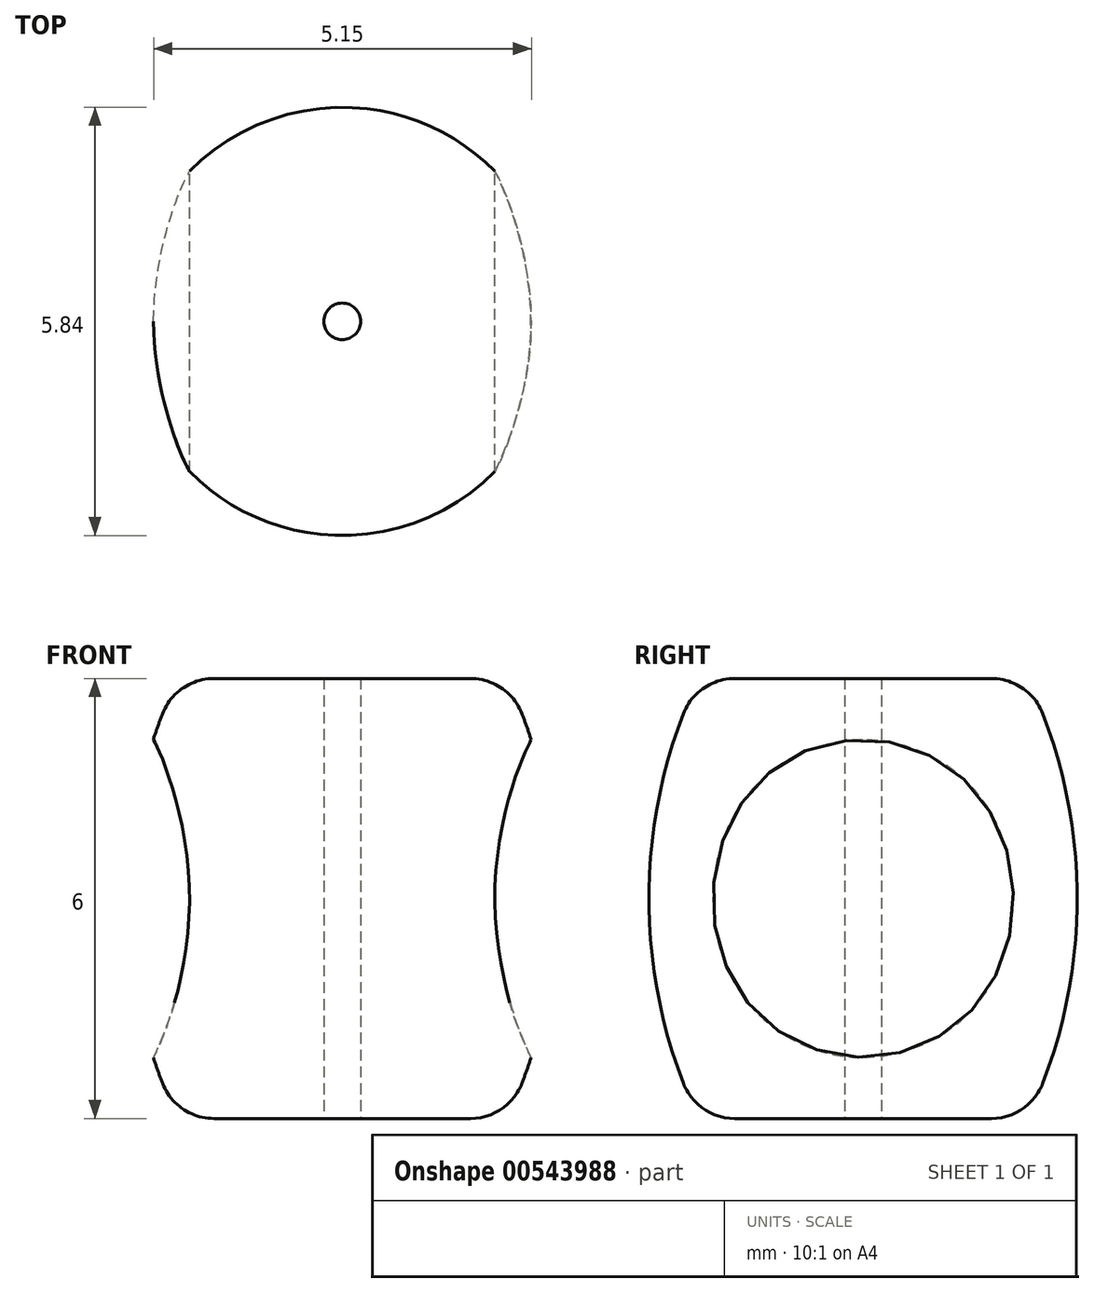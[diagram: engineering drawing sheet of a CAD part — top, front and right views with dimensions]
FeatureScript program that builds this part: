
annotation { "Feature Type Name" : "Feature", "Feature Type Description" : "" }
export const myFeature = defineFeature(function(context is Context, id is Id, definition is map)
    precondition{}
    {
        {
            var Q0;
            Q0=qCreatedBy(makeId("Front.planeOp"),FACE);
            var sketch = newSketch(context, id + "F0", { "sketchPlane" : qUnion([Q0])});
            skLineSegment(sketch, "E0", {"start": v(0.25, 0) * mm, "end": v(0.25, 6) * mm});
            skLineSegment(sketch, "E1", {"start": v(0.25, 0) * mm, "end": v(1.75, 0) * mm});
            skArc(sketch, "E2", {"start": v(1.75, 0) * mm, "mid": v(2.17, 0.13) * mm, "end": v(2.45, 0.48) * mm});
            skLineSegment(sketch, "E3", {"start": v(0, 0) * mm, "end": v(0, 8.8) * mm});
            skArc(sketch, "E4", {"start": v(2.45, 0.48) * mm, "mid": v(2.92, 3) * mm, "end": v(2.45, 5.52) * mm});
            skLineSegment(sketch, "E5", {"start": v(0.25, 6) * mm, "end": v(1.75, 6) * mm});
            skArc(sketch, "E6", {"start": v(1.75, 6) * mm, "mid": v(2.17, 5.87) * mm, "end": v(2.45, 5.52) * mm});
            skLineSegment(sketch, "E7", {"start": v(1.75, 0) * mm, "end": v(1.75, 6) * mm, "construction": true});
            skSolve(sketch);
        }
        {
            var Q0;
            Q0=makeQuery(id+"F0.imprint","IMPRINT",FACE,{"disambiguationData":[TD([[makeQuery(id+"F0.imprint","IMPRINT",EDGE,{"derivedFrom":sQuery(id+"F0.wireOp",EDGE,"E0")}),-1.0]])]});
            var Q1;
            Q1=sQuery(id+"F0.wireOp",EDGE,"E3");
            revolve(context, id + "F1", {"entities" : qUnion([Q0]), "axis" : qUnion([Q1]), "revolveType" : RevolveType.FULL});
        }
        {
            var Q0;
            Q0=qCreatedBy(makeId("Front.planeOp"),FACE);
            var sketch = newSketch(context, id + "F2", { "sketchPlane" : qUnion([Q0])});
            skArc(sketch, "E8", {"start": v(2.75, 5.5) * mm, "mid": v(2.08, 3) * mm, "end": v(2.75, 0.5) * mm});
            skLineSegment(sketch, "E9", {"start": v(2.75, 5.5) * mm, "end": v(2.75, 0.5) * mm, "construction": true});
            skLineSegment(sketch, "E10", {"start": v(2.75, 5.5) * mm, "end": v(3.75, 5.5) * mm});
            skLineSegment(sketch, "E11", {"start": v(3.75, 5.5) * mm, "end": v(3.75, 0.5) * mm});
            skLineSegment(sketch, "E12", {"start": v(3.75, 0.5) * mm, "end": v(2.75, 0.5) * mm});
            skSolve(sketch);
        }
        {
            var Q0;
            Q0=makeQuery(id+"F2.imprint","IMPRINT",FACE,{"disambiguationData":[TD([[makeQuery(id+"F2.imprint","IMPRINT",EDGE,{"derivedFrom":sQuery(id+"F2.wireOp",EDGE,"E8")}),1.0]])]});
            extrude(context, id + "F3", {"entities" : qUnion([Q0]), "depth" : 3 * mm, "offsetDistance" : 25 * mm, "hasSecondDirection" : true, "secondDirectionOppositeDirection" : true, "secondDirectionDepth" : 3 * mm});
        }
        {
            var Q0;
            Q0=makeQuery(id+"F3.opExtrude","SWEPT_BODY",BODY,{"disambiguationData":[OSD([sQuery(id+"F2.wireOp",EDGE,"E8"),sQuery(id+"F2.wireOp",EDGE,"E10"),sQuery(id+"F2.wireOp",EDGE,"E11"),sQuery(id+"F2.wireOp",EDGE,"E12")])]});
            var Q1;
            Q1=qCreatedBy(makeId("Right.planeOp"),FACE);
            mirror(context, id + "F4", {"entities" : qUnion([Q0]), "mirrorPlane" : qUnion([Q1])});
        }
        {
            var Q0;
            Q0=makeQuery(id+"F3.opExtrude","SWEPT_BODY",BODY,{"disambiguationData":[OSD([sQuery(id+"F2.wireOp",EDGE,"E8"),sQuery(id+"F2.wireOp",EDGE,"E10"),sQuery(id+"F2.wireOp",EDGE,"E11"),sQuery(id+"F2.wireOp",EDGE,"E12")])]});
            var Q1;
            Q1=makeQuery(id+"F4.opPattern","COPY",BODY,{"derivedFrom":makeQuery(id+"F3.opExtrude","SWEPT_BODY",BODY,{"disambiguationData":[OSD([sQuery(id+"F2.wireOp",EDGE,"E8"),sQuery(id+"F2.wireOp",EDGE,"E10"),sQuery(id+"F2.wireOp",EDGE,"E11"),sQuery(id+"F2.wireOp",EDGE,"E12")])]}),"instanceName":"1"});
            var Q2;
            Q2=makeQuery(id+"F1.opRevolve","SWEPT_BODY",BODY,{"disambiguationData":[OSD([sQuery(id+"F0.wireOp",EDGE,"E0"),sQuery(id+"F0.wireOp",EDGE,"E1"),sQuery(id+"F0.wireOp",EDGE,"E2"),sQuery(id+"F0.wireOp",EDGE,"E4"),sQuery(id+"F0.wireOp",EDGE,"E5"),sQuery(id+"F0.wireOp",EDGE,"E6")])]});
            booleanBodies(context, id + "F5", {"operationType" : BooleanOperationType.SUBTRACTION, "tools" : qUnion([Q0, Q1]), "targets" : qUnion([Q2])});
        }
    });
